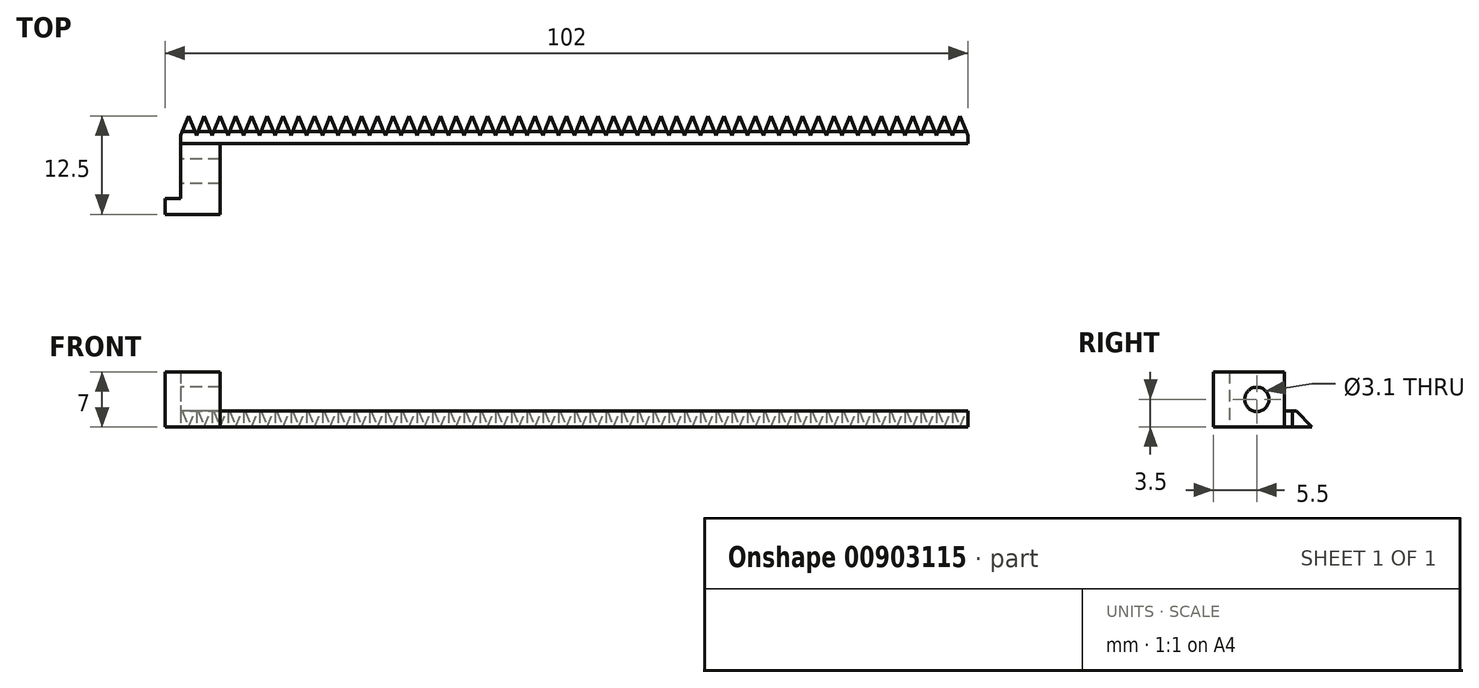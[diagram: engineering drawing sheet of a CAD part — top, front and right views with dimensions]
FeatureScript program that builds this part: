
annotation { "Feature Type Name" : "Feature", "Feature Type Description" : "" }
export const myFeature = defineFeature(function(context is Context, id is Id, definition is map)
    precondition{}
    {
        {
            var Q0;
            Q0=qCreatedBy(makeId("Top.planeOp"),FACE);
            var sketch = newSketch(context, id + "F0", { "sketchPlane" : qUnion([Q0])});
            skLineSegment(sketch, "E0", {"start": v(0, 1) * mm, "end": v(1, 3.5) * mm});
            skLineSegment(sketch, "E1", {"start": v(1, 3.5) * mm, "end": v(2, 1) * mm});
            skLineSegment(sketch, "E2.1.0.0", {"start": v(2, 1) * mm, "end": v(3, 3.5) * mm});
            skLineSegment(sketch, "E2.1.0.1", {"start": v(3, 3.5) * mm, "end": v(4, 1) * mm});
            skLineSegment(sketch, "E2.2.0.0", {"start": v(4, 1) * mm, "end": v(5, 3.5) * mm});
            skLineSegment(sketch, "E2.2.0.1", {"start": v(5, 3.5) * mm, "end": v(6, 1) * mm});
            skLineSegment(sketch, "E2.3.0.0", {"start": v(6, 1) * mm, "end": v(7, 3.5) * mm});
            skLineSegment(sketch, "E2.3.0.1", {"start": v(7, 3.5) * mm, "end": v(8, 1) * mm});
            skLineSegment(sketch, "E2.4.0.0", {"start": v(8, 1) * mm, "end": v(9, 3.5) * mm});
            skLineSegment(sketch, "E2.4.0.1", {"start": v(9, 3.5) * mm, "end": v(10, 1) * mm});
            skLineSegment(sketch, "E2.5.0.0", {"start": v(10, 1) * mm, "end": v(11, 3.5) * mm});
            skLineSegment(sketch, "E2.5.0.1", {"start": v(11, 3.5) * mm, "end": v(12, 1) * mm});
            skLineSegment(sketch, "E2.6.0.0", {"start": v(12, 1) * mm, "end": v(13, 3.5) * mm});
            skLineSegment(sketch, "E2.6.0.1", {"start": v(13, 3.5) * mm, "end": v(14, 1) * mm});
            skLineSegment(sketch, "E2.7.0.0", {"start": v(14, 1) * mm, "end": v(15, 3.5) * mm});
            skLineSegment(sketch, "E2.7.0.1", {"start": v(15, 3.5) * mm, "end": v(16, 1) * mm});
            skLineSegment(sketch, "E2.8.0.0", {"start": v(16, 1) * mm, "end": v(17, 3.5) * mm});
            skLineSegment(sketch, "E2.8.0.1", {"start": v(17, 3.5) * mm, "end": v(18, 1) * mm});
            skLineSegment(sketch, "E2.9.0.0", {"start": v(18, 1) * mm, "end": v(19, 3.5) * mm});
            skLineSegment(sketch, "E2.9.0.1", {"start": v(19, 3.5) * mm, "end": v(20, 1) * mm});
            skLineSegment(sketch, "E2.10.0.0", {"start": v(20, 1) * mm, "end": v(21, 3.5) * mm});
            skLineSegment(sketch, "E2.10.0.1", {"start": v(21, 3.5) * mm, "end": v(22, 1) * mm});
            skLineSegment(sketch, "E2.11.0.0", {"start": v(22, 1) * mm, "end": v(23, 3.5) * mm});
            skLineSegment(sketch, "E2.11.0.1", {"start": v(23, 3.5) * mm, "end": v(24, 1) * mm});
            skLineSegment(sketch, "E2.12.0.0", {"start": v(24, 1) * mm, "end": v(25, 3.5) * mm});
            skLineSegment(sketch, "E2.12.0.1", {"start": v(25, 3.5) * mm, "end": v(26, 1) * mm});
            skLineSegment(sketch, "E2.13.0.0", {"start": v(26, 1) * mm, "end": v(27, 3.5) * mm});
            skLineSegment(sketch, "E2.13.0.1", {"start": v(27, 3.5) * mm, "end": v(28, 1) * mm});
            skLineSegment(sketch, "E2.14.0.0", {"start": v(28, 1) * mm, "end": v(29, 3.5) * mm});
            skLineSegment(sketch, "E2.14.0.1", {"start": v(29, 3.5) * mm, "end": v(30, 1) * mm});
            skLineSegment(sketch, "E2.15.0.0", {"start": v(30, 1) * mm, "end": v(31, 3.5) * mm});
            skLineSegment(sketch, "E2.15.0.1", {"start": v(31, 3.5) * mm, "end": v(32, 1) * mm});
            skLineSegment(sketch, "E2.16.0.0", {"start": v(32, 1) * mm, "end": v(33, 3.5) * mm});
            skLineSegment(sketch, "E2.16.0.1", {"start": v(33, 3.5) * mm, "end": v(34, 1) * mm});
            skLineSegment(sketch, "E2.17.0.0", {"start": v(34, 1) * mm, "end": v(35, 3.5) * mm});
            skLineSegment(sketch, "E2.17.0.1", {"start": v(35, 3.5) * mm, "end": v(36, 1) * mm});
            skLineSegment(sketch, "E2.18.0.0", {"start": v(36, 1) * mm, "end": v(37, 3.5) * mm});
            skLineSegment(sketch, "E2.18.0.1", {"start": v(37, 3.5) * mm, "end": v(38, 1) * mm});
            skLineSegment(sketch, "E2.19.0.0", {"start": v(38, 1) * mm, "end": v(39, 3.5) * mm});
            skLineSegment(sketch, "E2.19.0.1", {"start": v(39, 3.5) * mm, "end": v(40, 1) * mm});
            skLineSegment(sketch, "E2.direction1", {"start": v(0, 1) * mm, "end": v(2, 1) * mm, "construction": true});
            skLineSegment(sketch, "E3", {"start": v(0, 1) * mm, "end": v(0, 0) * mm});
            skLineSegment(sketch, "E4", {"start": v(100, 0) * mm, "end": v(0, 0) * mm});
            skLineSegment(sketch, "E5.0.20.0", {"start": v(40, 1) * mm, "end": v(41, 3.5) * mm});
            skLineSegment(sketch, "E5.3.20.0", {"start": v(41, 3.5) * mm, "end": v(42, 1) * mm});
            skLineSegment(sketch, "E5.0.21.0", {"start": v(42, 1) * mm, "end": v(43, 3.5) * mm});
            skLineSegment(sketch, "E5.3.21.0", {"start": v(43, 3.5) * mm, "end": v(44, 1) * mm});
            skLineSegment(sketch, "E5.0.22.0", {"start": v(44, 1) * mm, "end": v(45, 3.5) * mm});
            skLineSegment(sketch, "E5.3.22.0", {"start": v(45, 3.5) * mm, "end": v(46, 1) * mm});
            skLineSegment(sketch, "E5.0.23.0", {"start": v(46, 1) * mm, "end": v(47, 3.5) * mm});
            skLineSegment(sketch, "E5.3.23.0", {"start": v(47, 3.5) * mm, "end": v(48, 1) * mm});
            skLineSegment(sketch, "E5.0.24.0", {"start": v(48, 1) * mm, "end": v(49, 3.5) * mm});
            skLineSegment(sketch, "E5.3.24.0", {"start": v(49, 3.5) * mm, "end": v(50, 1) * mm});
            skLineSegment(sketch, "E5.0.25.0", {"start": v(50, 1) * mm, "end": v(51, 3.5) * mm});
            skLineSegment(sketch, "E5.3.25.0", {"start": v(51, 3.5) * mm, "end": v(52, 1) * mm});
            skLineSegment(sketch, "E5.0.26.0", {"start": v(52, 1) * mm, "end": v(53, 3.5) * mm});
            skLineSegment(sketch, "E5.3.26.0", {"start": v(53, 3.5) * mm, "end": v(54, 1) * mm});
            skLineSegment(sketch, "E5.0.27.0", {"start": v(54, 1) * mm, "end": v(55, 3.5) * mm});
            skLineSegment(sketch, "E5.3.27.0", {"start": v(55, 3.5) * mm, "end": v(56, 1) * mm});
            skLineSegment(sketch, "E5.0.28.0", {"start": v(56, 1) * mm, "end": v(57, 3.5) * mm});
            skLineSegment(sketch, "E5.3.28.0", {"start": v(57, 3.5) * mm, "end": v(58, 1) * mm});
            skLineSegment(sketch, "E5.0.29.0", {"start": v(58, 1) * mm, "end": v(59, 3.5) * mm});
            skLineSegment(sketch, "E5.3.29.0", {"start": v(59, 3.5) * mm, "end": v(60, 1) * mm});
            skLineSegment(sketch, "E5.0.30.0", {"start": v(60, 1) * mm, "end": v(61, 3.5) * mm});
            skLineSegment(sketch, "E5.3.30.0", {"start": v(61, 3.5) * mm, "end": v(62, 1) * mm});
            skLineSegment(sketch, "E5.0.31.0", {"start": v(62, 1) * mm, "end": v(63, 3.5) * mm});
            skLineSegment(sketch, "E5.3.31.0", {"start": v(63, 3.5) * mm, "end": v(64, 1) * mm});
            skLineSegment(sketch, "E5.0.32.0", {"start": v(64, 1) * mm, "end": v(65, 3.5) * mm});
            skLineSegment(sketch, "E5.3.32.0", {"start": v(65, 3.5) * mm, "end": v(66, 1) * mm});
            skLineSegment(sketch, "E5.0.33.0", {"start": v(66, 1) * mm, "end": v(67, 3.5) * mm});
            skLineSegment(sketch, "E5.3.33.0", {"start": v(67, 3.5) * mm, "end": v(68, 1) * mm});
            skLineSegment(sketch, "E5.0.34.0", {"start": v(68, 1) * mm, "end": v(69, 3.5) * mm});
            skLineSegment(sketch, "E5.3.34.0", {"start": v(69, 3.5) * mm, "end": v(70, 1) * mm});
            skLineSegment(sketch, "E5.0.35.0", {"start": v(70, 1) * mm, "end": v(71, 3.5) * mm});
            skLineSegment(sketch, "E5.3.35.0", {"start": v(71, 3.5) * mm, "end": v(72, 1) * mm});
            skLineSegment(sketch, "E5.0.36.0", {"start": v(72, 1) * mm, "end": v(73, 3.5) * mm});
            skLineSegment(sketch, "E5.3.36.0", {"start": v(73, 3.5) * mm, "end": v(74, 1) * mm});
            skLineSegment(sketch, "E5.0.37.0", {"start": v(74, 1) * mm, "end": v(75, 3.5) * mm});
            skLineSegment(sketch, "E5.3.37.0", {"start": v(75, 3.5) * mm, "end": v(76, 1) * mm});
            skLineSegment(sketch, "E5.0.38.0", {"start": v(76, 1) * mm, "end": v(77, 3.5) * mm});
            skLineSegment(sketch, "E5.3.38.0", {"start": v(77, 3.5) * mm, "end": v(78, 1) * mm});
            skLineSegment(sketch, "E5.0.39.0", {"start": v(78, 1) * mm, "end": v(79, 3.5) * mm});
            skLineSegment(sketch, "E5.3.39.0", {"start": v(79, 3.5) * mm, "end": v(80, 1) * mm});
            skLineSegment(sketch, "E5.0.40.0", {"start": v(80, 1) * mm, "end": v(81, 3.5) * mm});
            skLineSegment(sketch, "E5.3.40.0", {"start": v(81, 3.5) * mm, "end": v(82, 1) * mm});
            skLineSegment(sketch, "E5.0.41.0", {"start": v(82, 1) * mm, "end": v(83, 3.5) * mm});
            skLineSegment(sketch, "E5.3.41.0", {"start": v(83, 3.5) * mm, "end": v(84, 1) * mm});
            skLineSegment(sketch, "E5.0.42.0", {"start": v(84, 1) * mm, "end": v(85, 3.5) * mm});
            skLineSegment(sketch, "E5.3.42.0", {"start": v(85, 3.5) * mm, "end": v(86, 1) * mm});
            skLineSegment(sketch, "E5.0.43.0", {"start": v(86, 1) * mm, "end": v(87, 3.5) * mm});
            skLineSegment(sketch, "E5.3.43.0", {"start": v(87, 3.5) * mm, "end": v(88, 1) * mm});
            skLineSegment(sketch, "E5.0.44.0", {"start": v(88, 1) * mm, "end": v(89, 3.5) * mm});
            skLineSegment(sketch, "E5.3.44.0", {"start": v(89, 3.5) * mm, "end": v(90, 1) * mm});
            skLineSegment(sketch, "E5.0.45.0", {"start": v(90, 1) * mm, "end": v(91, 3.5) * mm});
            skLineSegment(sketch, "E5.3.45.0", {"start": v(91, 3.5) * mm, "end": v(92, 1) * mm});
            skLineSegment(sketch, "E5.0.46.0", {"start": v(92, 1) * mm, "end": v(93, 3.5) * mm});
            skLineSegment(sketch, "E5.3.46.0", {"start": v(93, 3.5) * mm, "end": v(94, 1) * mm});
            skLineSegment(sketch, "E5.0.47.0", {"start": v(94, 1) * mm, "end": v(95, 3.5) * mm});
            skLineSegment(sketch, "E5.3.47.0", {"start": v(95, 3.5) * mm, "end": v(96, 1) * mm});
            skLineSegment(sketch, "E5.0.48.0", {"start": v(96, 1) * mm, "end": v(97, 3.5) * mm});
            skLineSegment(sketch, "E5.3.48.0", {"start": v(97, 3.5) * mm, "end": v(98, 1) * mm});
            skLineSegment(sketch, "E5.0.49.0", {"start": v(98, 1) * mm, "end": v(99, 3.5) * mm});
            skLineSegment(sketch, "E5.3.49.0", {"start": v(99, 3.5) * mm, "end": v(100, 1) * mm});
            skLineSegment(sketch, "E6", {"start": v(100, 1) * mm, "end": v(100, 0) * mm});
            skSolve(sketch);
        }
        {
            var Q0;
            Q0=makeQuery(id+"F0.imprint","IMPRINT",FACE,{"disambiguationData":[TD([[makeQuery(id+"F0.imprint","IMPRINT",EDGE,{"derivedFrom":sQuery(id+"F0.wireOp",EDGE,"E0")}),-1.0]])]});
            extrude(context, id + "F1", {"entities" : qUnion([Q0]), "depth" : 2 * mm});
        }
        {
            var Q0;
            Q0=qCreatedBy(makeId("Right.planeOp"),FACE);
            var sketch = newSketch(context, id + "F2", { "sketchPlane" : qUnion([Q0])});
            skLineSegment(sketch, "E7", {"start": v(0, 0) * mm, "end": v(0, 3.5) * mm});
            skLineSegment(sketch, "E8", {"start": v(0, 3.5) * mm, "end": v(3.5, 0) * mm});
            skLineSegment(sketch, "E9", {"start": v(3.5, 0) * mm, "end": v(0, 0) * mm});
            skPoint(sketch, "E10.0", {"position": v(3.5, 0) * mm});
            skSolve(sketch);
        }
        {
            var Q0;
            Q0=makeQuery(id+"F2.imprint","IMPRINT",FACE,{"disambiguationData":[TD([[makeQuery(id+"F2.imprint","IMPRINT",EDGE,{"derivedFrom":sQuery(id+"F2.wireOp",EDGE,"E7")}),-1.0]])]});
            extrude(context, id + "F3", {"entities" : qUnion([Q0]), "operationType" : NewBodyOperationType.INTERSECT, "endBound" : BoundingType.THROUGH_ALL, "depth" : 25 * mm});
        }
        {
            var Q0;
            Q0=qCreatedBy(makeId("Top.planeOp"),FACE);
            var sketch = newSketch(context, id + "F4", { "sketchPlane" : qUnion([Q0])});
            skLineSegment(sketch, "E11", {"start": v(0, 0) * mm, "end": v(0, -7) * mm});
            skLineSegment(sketch, "E12", {"start": v(0, -7) * mm, "end": v(5, -7) * mm});
            skLineSegment(sketch, "E13", {"start": v(5, -7) * mm, "end": v(5, 0) * mm});
            skLineSegment(sketch, "E14", {"start": v(0, 0) * mm, "end": v(5, 0) * mm});
            skLineSegment(sketch, "E15", {"start": v(5, -7) * mm, "end": v(5, -9) * mm});
            skLineSegment(sketch, "E16", {"start": v(5, -9) * mm, "end": v(-2, -9) * mm});
            skLineSegment(sketch, "E17", {"start": v(-2, -9) * mm, "end": v(-2, -7) * mm});
            skLineSegment(sketch, "E18", {"start": v(-2, -7) * mm, "end": v(0, -7) * mm});
            skSolve(sketch);
        }
        {
            var Q0;
            Q0=makeQuery(id+"F4.imprint","IMPRINT",FACE,{"disambiguationData":[TD([[makeQuery(id+"F4.imprint","IMPRINT",EDGE,{"derivedFrom":sQuery(id+"F4.wireOp",EDGE,"E11")}),1.0]])]});
            var Q1;
            Q1=makeQuery(id+"F4.imprint","IMPRINT",FACE,{"disambiguationData":[TD([[makeQuery(id+"F4.imprint","IMPRINT",EDGE,{"derivedFrom":sQuery(id+"F4.wireOp",EDGE,"E12")}),-1.0]])]});
            extrude(context, id + "F5", {"entities" : qUnion([Q0, Q1]), "operationType" : NewBodyOperationType.ADD, "depth" : 7 * mm});
        }
        {
            var Q0;
            Q0=makeQuery(id+"F5.boolean.opBoolean","MERGE",FACE,{"derivedFrom":[makeQuery(id+"F1.opExtrude","SWEPT_FACE",FACE,{"disambiguationData":[OSD([sQuery(id+"F0.wireOp",EDGE,"E3")])]}),makeQuery(id+"F5.opExtrude","SWEPT_FACE",FACE,{"disambiguationData":[OSD([sQuery(id+"F4.wireOp",EDGE,"E11")])]})]});
            var sketch = newSketch(context, id + "F6", { "sketchPlane" : qUnion([Q0])});
            skPoint(sketch, "E19.0", {"position": v(3.5, 7) * mm});
            skPoint(sketch, "E19.1", {"position": v(7, 3.5) * mm});
            skLineSegment(sketch, "E20", {"start": v(7, 3.5) * mm, "end": v(3.5, 3.5) * mm, "construction": true});
            skCircle(sketch, "E21", {"center": v(3.5, 3.5) * mm, "radius": 1.55 * mm});
            skSolve(sketch);
        }
        {
            var Q0;
            Q0=makeQuery(id+"F6.imprint","IMPRINT",FACE,{"disambiguationData":[TD([[makeQuery(id+"F6.imprint","IMPRINT",EDGE,{"derivedFrom":sQuery(id+"F6.wireOp",EDGE,"E21")}),1.0]])]});
            var Q1;
            Q1=makeQuery(id+"F5.opExtrude","SWEPT_FACE",FACE,{"disambiguationData":[OSD([sQuery(id+"F4.wireOp",EDGE,"E13"),sQuery(id+"F4.wireOp",EDGE,"E15")])]});
            extrude(context, id + "F7", {"entities" : qUnion([Q0]), "operationType" : NewBodyOperationType.REMOVE, "endBound" : BoundingType.UP_TO_SURFACE, "oppositeDirection" : true, "endBoundEntityFace" : qUnion([Q1]), "depth" : 25 * mm});
        }
    });
